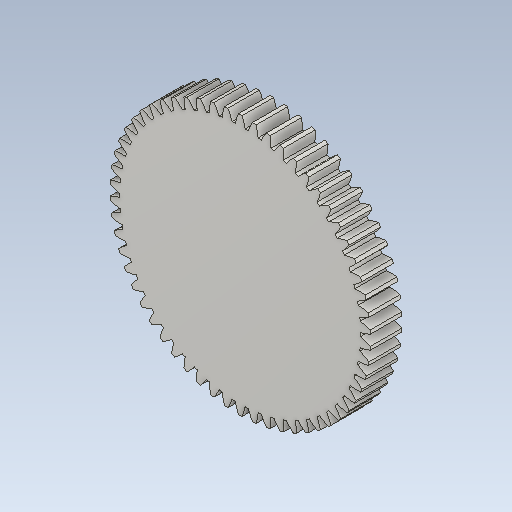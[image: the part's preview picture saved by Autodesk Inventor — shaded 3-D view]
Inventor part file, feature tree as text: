
AUTODESK INVENTOR PART (.ipt)
format: ipt  version: 2021 (Build 250183000, 183)  size: 390,656 bytes
history: native  units: mm (DEFAULTED — no unit token found)
features: plane x3, other x3, sketch x2, extrude x1
ambient origin geometry x8: Origin, YZ Plane, XZ Plane, XY Plane, X Axis, Y Axis, Z Axis, Center Point
bodies: Solid1 (feature_tree)
feature tree (9):
  extrude  "Extrusion1"  Depth=20.0mm TaperAngle=0.0deg
  plane  "Work Plane2"
  plane  "Work Plane8"
  plane  "Work Plane9"
  other  "Цилиндрическое зубчатое зацепление"
  sketch  "Sketch1"  dims[d0=165.0mm d1=20.0mm d2=0.0mm]
  sketch  "Sketch2"  dims[d3=159.5mm d4=10.0mm d5=0.0mm d16=320.0mm d17=0.0mm d34=0.541654mm d39=0.0mm d41=0.0mm d43=320.0mm d46=320.0mm d47=0.0mm d48=0.0mm]
  other  "Srf1"
  other  "Средний диаметр"
